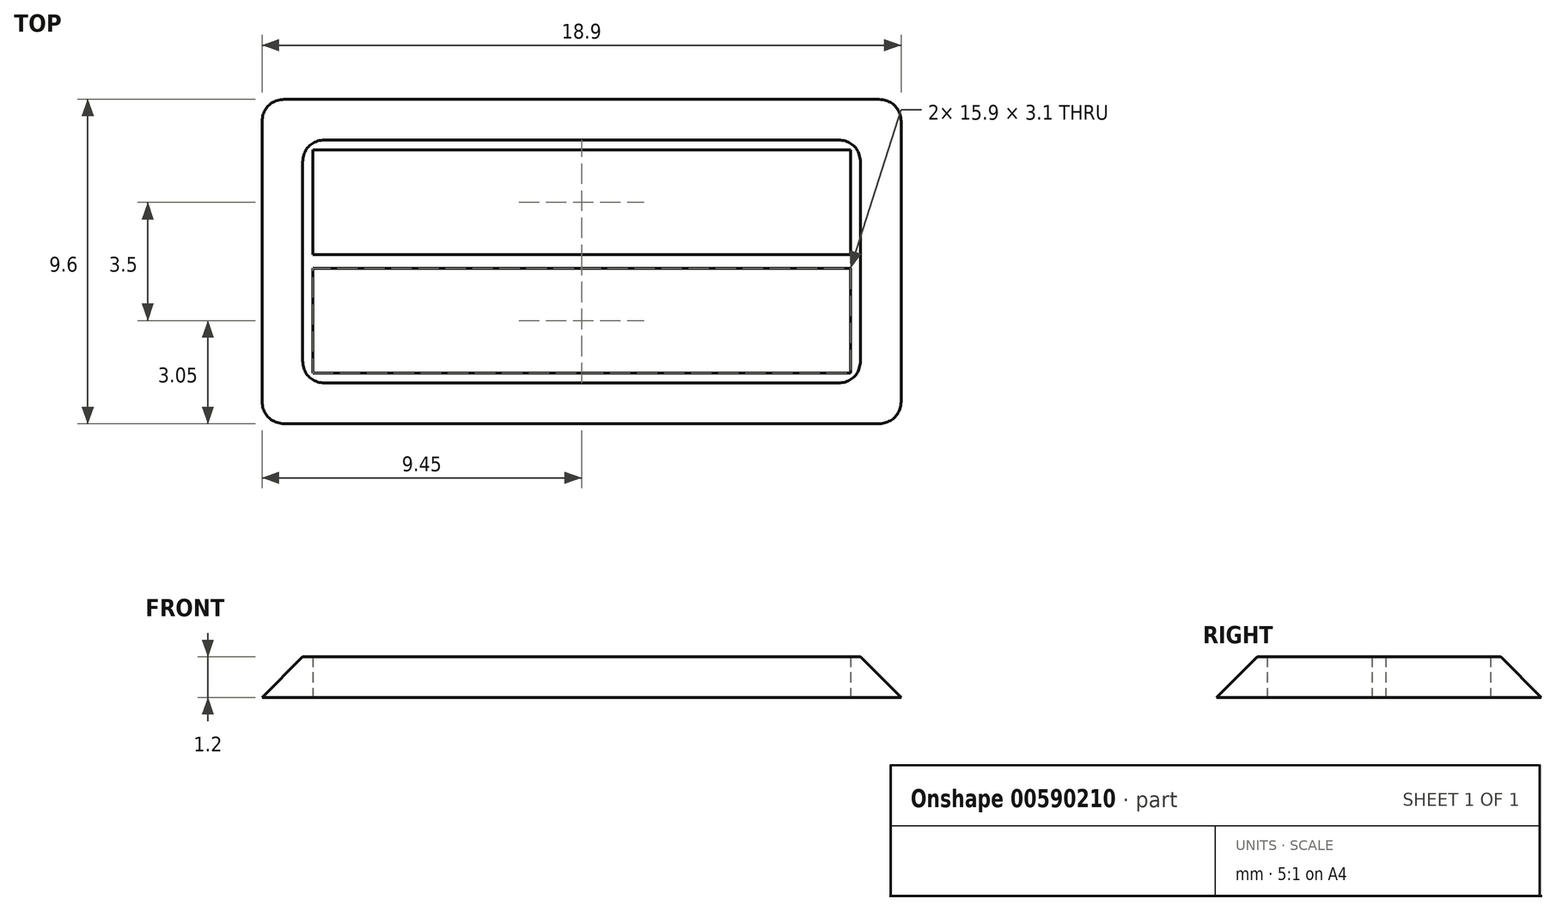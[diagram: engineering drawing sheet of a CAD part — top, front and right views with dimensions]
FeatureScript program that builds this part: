
annotation { "Feature Type Name" : "Feature", "Feature Type Description" : "" }
export const myFeature = defineFeature(function(context is Context, id is Id, definition is map)
    precondition{}
    {
        {
            var Q0;
            Q0=qCreatedBy(makeId("Top.planeOp"),FACE);
            var sketch = newSketch(context, id + "F0", { "sketchPlane" : qUnion([Q0])});
            skPoint(sketch, "E0.middle", {"position": v(0, 0) * mm});
            skLineSegment(sketch, "E1.bottom", {"start": v(-7.95, 3.3) * mm, "end": v(7.95, 3.3) * mm});
            skLineSegment(sketch, "E1.top", {"start": v(-7.95, 0.2) * mm, "end": v(7.95, 0.2) * mm});
            skLineSegment(sketch, "E1.left", {"start": v(-7.95, 3.3) * mm, "end": v(-7.95, 0.2) * mm});
            skLineSegment(sketch, "E1.right", {"start": v(7.95, 3.3) * mm, "end": v(7.95, 0.2) * mm});
            skPoint(sketch, "E1.middle", {"position": v(0, 1.75) * mm});
            skLineSegment(sketch, "E2.bottom", {"start": v(-7.95, -0.2) * mm, "end": v(7.95, -0.2) * mm});
            skLineSegment(sketch, "E2.top", {"start": v(-7.95, -3.3) * mm, "end": v(7.95, -3.3) * mm});
            skLineSegment(sketch, "E2.left", {"start": v(-7.95, -0.2) * mm, "end": v(-7.95, -3.3) * mm});
            skLineSegment(sketch, "E2.right", {"start": v(7.95, -0.2) * mm, "end": v(7.95, -3.3) * mm});
            skPoint(sketch, "E2.middle", {"position": v(0, -1.75) * mm});
            skLineSegment(sketch, "E3.bottom", {"start": v(-9.45, 4.8) * mm, "end": v(9.45, 4.8) * mm});
            skLineSegment(sketch, "E3.top", {"start": v(-9.45, -4.8) * mm, "end": v(9.45, -4.8) * mm});
            skLineSegment(sketch, "E3.left", {"start": v(-9.45, 4.8) * mm, "end": v(-9.45, -4.8) * mm});
            skLineSegment(sketch, "E3.right", {"start": v(9.45, 4.8) * mm, "end": v(9.45, -4.8) * mm});
            skSolve(sketch);
        }
        {
            var Q0;
            Q0=makeQuery(id+"F0.imprint","IMPRINT",FACE,{"disambiguationData":[TD([[makeQuery(id+"F0.imprint","IMPRINT",EDGE,{"derivedFrom":sQuery(id+"F0.wireOp",EDGE,"E1.bottom")}),1.0]])]});
            extrude(context, id + "F1", {"entities" : qUnion([Q0]), "depth" : 1.2 * mm, "offsetDistance" : 25 * mm});
        }
        {
            var Q0;
            Q0=makeQuery(id+"F1.opExtrude","CAP_EDGE",EDGE,{"disambiguationData":[OSD([sQuery(id+"F0.wireOp",EDGE,"E3.top")])],"isStart":false});
            var Q1;
            Q1=makeQuery(id+"F1.opExtrude","CAP_EDGE",EDGE,{"disambiguationData":[OSD([sQuery(id+"F0.wireOp",EDGE,"E3.left")])],"isStart":false});
            var Q2;
            Q2=makeQuery(id+"F1.opExtrude","CAP_EDGE",EDGE,{"disambiguationData":[OSD([sQuery(id+"F0.wireOp",EDGE,"E3.right")])],"isStart":false});
            var Q3;
            Q3=makeQuery(id+"F1.opExtrude","CAP_EDGE",EDGE,{"disambiguationData":[OSD([sQuery(id+"F0.wireOp",EDGE,"E3.bottom")])],"isStart":false});
            chamfer(context, id + "F2", {"entities" : qUnion([Q0, Q1, Q2, Q3]), "width" : 1.2 * mm});
        }
        {
            var Q0;
            Q0=makeQuery(id+"F2.opChamfer","BLEND_EDGE",EDGE,{"blendedFrom":[makeQuery(id+"F1.opExtrude","CAP_EDGE",EDGE,{"disambiguationData":[OSD([sQuery(id+"F0.wireOp",EDGE,"E3.top")])],"isStart":false}),makeQuery(id+"F1.opExtrude","CAP_EDGE",EDGE,{"disambiguationData":[OSD([sQuery(id+"F0.wireOp",EDGE,"E3.left")])],"isStart":false})],"blendedInto":[]});
            var Q1;
            Q1=makeQuery(id+"F2.opChamfer","BLEND_EDGE",EDGE,{"blendedFrom":[makeQuery(id+"F1.opExtrude","CAP_EDGE",EDGE,{"disambiguationData":[OSD([sQuery(id+"F0.wireOp",EDGE,"E3.top")])],"isStart":false}),makeQuery(id+"F1.opExtrude","CAP_EDGE",EDGE,{"disambiguationData":[OSD([sQuery(id+"F0.wireOp",EDGE,"E3.right")])],"isStart":false})],"blendedInto":[]});
            var Q2;
            Q2=makeQuery(id+"F2.opChamfer","BLEND_EDGE",EDGE,{"blendedFrom":[makeQuery(id+"F1.opExtrude","CAP_EDGE",EDGE,{"disambiguationData":[OSD([sQuery(id+"F0.wireOp",EDGE,"E3.bottom")])],"isStart":false}),makeQuery(id+"F1.opExtrude","CAP_EDGE",EDGE,{"disambiguationData":[OSD([sQuery(id+"F0.wireOp",EDGE,"E3.right")])],"isStart":false})],"blendedInto":[]});
            var Q3;
            Q3=makeQuery(id+"F2.opChamfer","BLEND_EDGE",EDGE,{"blendedFrom":[makeQuery(id+"F1.opExtrude","CAP_EDGE",EDGE,{"disambiguationData":[OSD([sQuery(id+"F0.wireOp",EDGE,"E3.bottom")])],"isStart":false}),makeQuery(id+"F1.opExtrude","CAP_EDGE",EDGE,{"disambiguationData":[OSD([sQuery(id+"F0.wireOp",EDGE,"E3.left")])],"isStart":false})],"blendedInto":[]});
            fillet(context, id + "F3", {"entities" : qUnion([Q0, Q1, Q2, Q3]), "radius" : 1 * mm, "tangentPropagation" : true, "allowEdgeOverflow" : false});
        }
    });
